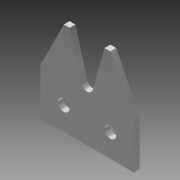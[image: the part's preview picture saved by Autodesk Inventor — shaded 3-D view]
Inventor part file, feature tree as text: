
AUTODESK INVENTOR PART (.ipt)
format: ipt  version: 2015 (Build 190159000, 159)  size: 136,704 bytes
history: native  units: in
note: dims shown in document units (in); Inventor stores cm internally (conversion verified against a paired STEP export)
features: sketch x4, extrude x3, projected_geometry x2, hole x1
ambient origin geometry x8: Origin, YZ Plane, XZ Plane, XY Plane, X Axis, Y Axis, Z Axis, Center Point
bodies: Solid1 (feature_tree)
feature tree (10):
  extrude  "Extrusion1"  Depth=2.0in
  hole  "Hole1"  [1 undecoded]
  extrude  "Extrusion2"  Depth=0.5in
  extrude  "Extrusion3"  Depth=1.0in
  sketch  "Sketch1"  dims[d0=2.0in d1=2.0in]
  sketch  "Sketch2"  dims[d2=0.125in d3=0.0in d4=0.5in]
  projected_geometry  "Projected Loop1"
  sketch  "Sketch3"  dims[d5=0.5in d6=0.5in]
  sketch  "Sketch4"  dims[d7=0.5in d8=0.25in d9=0.75in d10=0.375in d11=0.25in d12=0.5635in d13=1.0in d14=0.8108in d19=1.0in d20=1.0in d21=1.0in d22=0.5in d23=1.0in d24=0.0in d25=0.25in d26=0.875in d27=0.5in d28=0.125in d29=0.125in d30=1.0in d31=0.0in]
  projected_geometry  "Projected Loop2"
note: 1 required parameter value undecoded (feature->parameter linkage not recoverable at this tier; creation-order binding heuristic only, values carry confidence <= 0.55)
